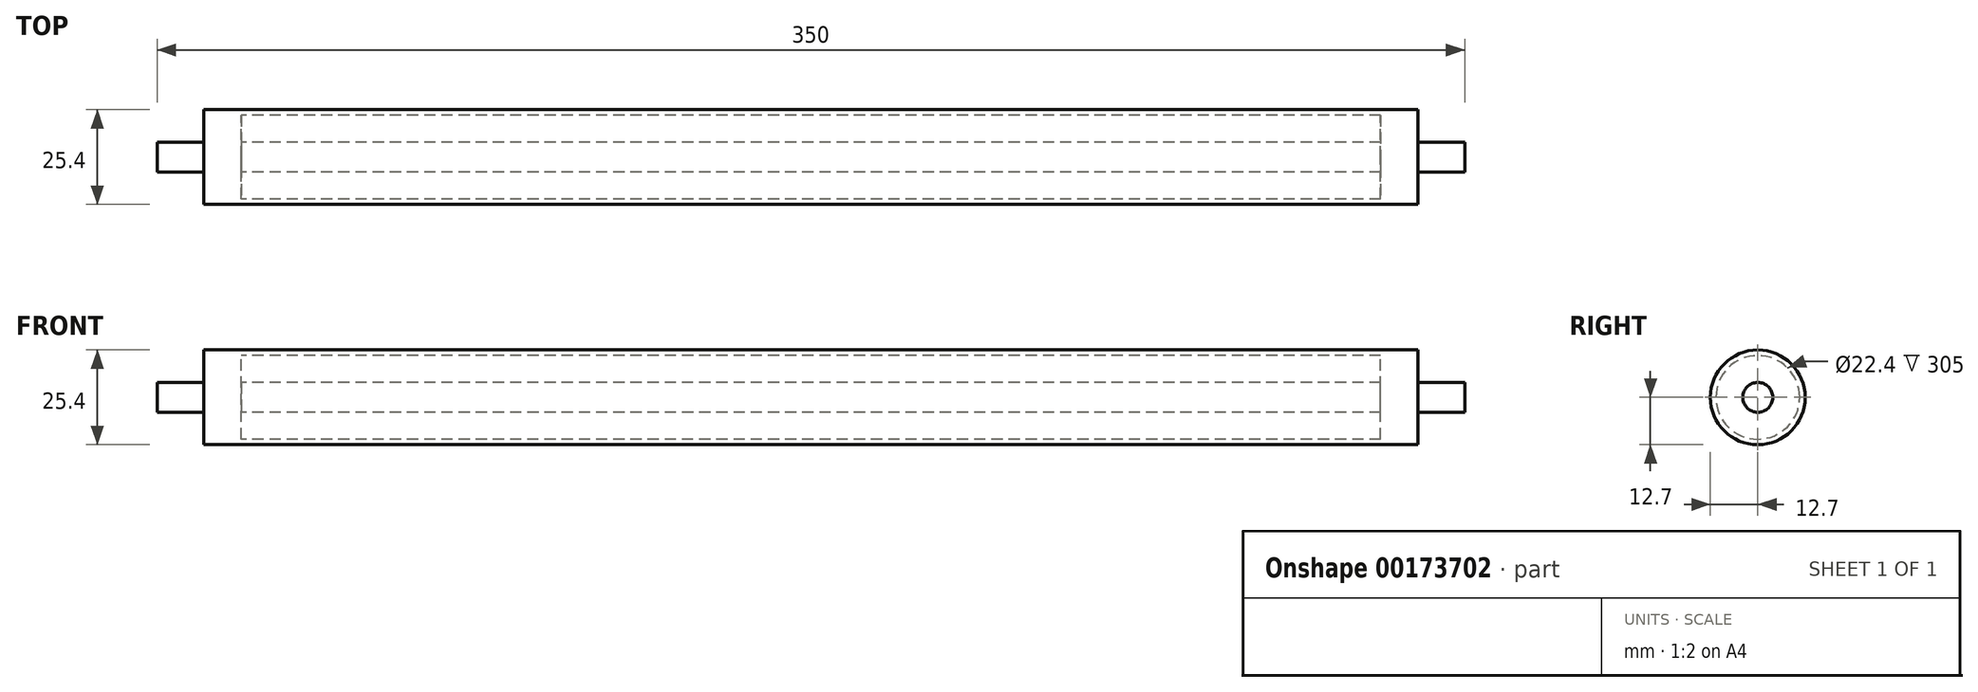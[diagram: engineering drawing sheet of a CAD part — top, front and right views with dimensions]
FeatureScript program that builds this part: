
annotation { "Feature Type Name" : "Feature", "Feature Type Description" : "" }
export const myFeature = defineFeature(function(context is Context, id is Id, definition is map)
    precondition{}
    {
        {
            var Q0;
            Q0=qCreatedBy(makeId("Right.planeOp"),FACE);
            var sketch = newSketch(context, id + "F0", { "sketchPlane" : qUnion([Q0])});
            skCircle(sketch, "E0", {"center": v(0, 0) * mm, "radius": 12.7 * mm});
            skCircle(sketch, "E1", {"center": v(0, 0) * mm, "radius": 11.2 * mm});
            skSolve(sketch);
        }
        {
            var Q0;
            Q0=qSketchRegion(id+"F0",true);
            extrude(context, id + "F1", {"entities" : qUnion([Q0]), "endBound" : BoundingType.SYMMETRIC, "depth" : 325 * mm});
        }
        {
            var Q0;
            Q0=qCreatedBy(makeId("Right.planeOp"),FACE);
            var sketch = newSketch(context, id + "F2", { "sketchPlane" : qUnion([Q0])});
            skCircle(sketch, "E2", {"center": v(0, 0) * mm, "radius": 4 * mm});
            skSolve(sketch);
        }
        {
            var Q0;
            Q0=qSketchRegion(id+"F2",true);
            extrude(context, id + "F3", {"entities" : qUnion([Q0]), "endBound" : BoundingType.SYMMETRIC, "depth" : 350 * mm});
        }
        {
            var Q0;
            Q0=makeQuery(id+"F1.opExtrude","CAP_FACE",FACE,{"disambiguationData":[OSD([sQuery(id+"F0.wireOp",EDGE,"E0"),sQuery(id+"F0.wireOp",EDGE,"E1")])],"isStart":false});
            var sketch = newSketch(context, id + "F4", { "sketchPlane" : qUnion([Q0])});
            skCircle(sketch, "E3.0", {"center": v(0, 0) * mm, "radius": 12.7 * mm});
            skSolve(sketch);
        }
        {
            var Q0;
            Q0=makeQuery(id+"F4.imprint","IMPRINT",FACE,{"disambiguationData":[TD([[makeQuery(id+"F4.imprint","IMPRINT",EDGE,{"derivedFrom":makeQuery(id+"F1.opExtrude","CAP_EDGE",EDGE,{"disambiguationData":[OSD([sQuery(id+"F0.wireOp",EDGE,"E1")])],"isStart":false})}),1.0]])]});
            extrude(context, id + "F5", {"entities" : qUnion([Q0]), "operationType" : NewBodyOperationType.ADD, "oppositeDirection" : true, "depth" : 10 * mm});
        }
        {
            var Q0;
            Q0=makeQuery(id+"F1.opExtrude","CAP_FACE",FACE,{"disambiguationData":[OSD([sQuery(id+"F0.wireOp",EDGE,"E0"),sQuery(id+"F0.wireOp",EDGE,"E1")])],"isStart":true});
            var sketch = newSketch(context, id + "F6", { "sketchPlane" : qUnion([Q0])});
            skCircle(sketch, "E4.0", {"center": v(0, 0) * mm, "radius": 11.2 * mm});
            skSolve(sketch);
        }
        {
            var Q0;
            Q0=qSketchRegion(id+"F6",true);
            extrude(context, id + "F7", {"entities" : qUnion([Q0]), "operationType" : NewBodyOperationType.ADD, "oppositeDirection" : true, "depth" : 10 * mm});
        }
    });
